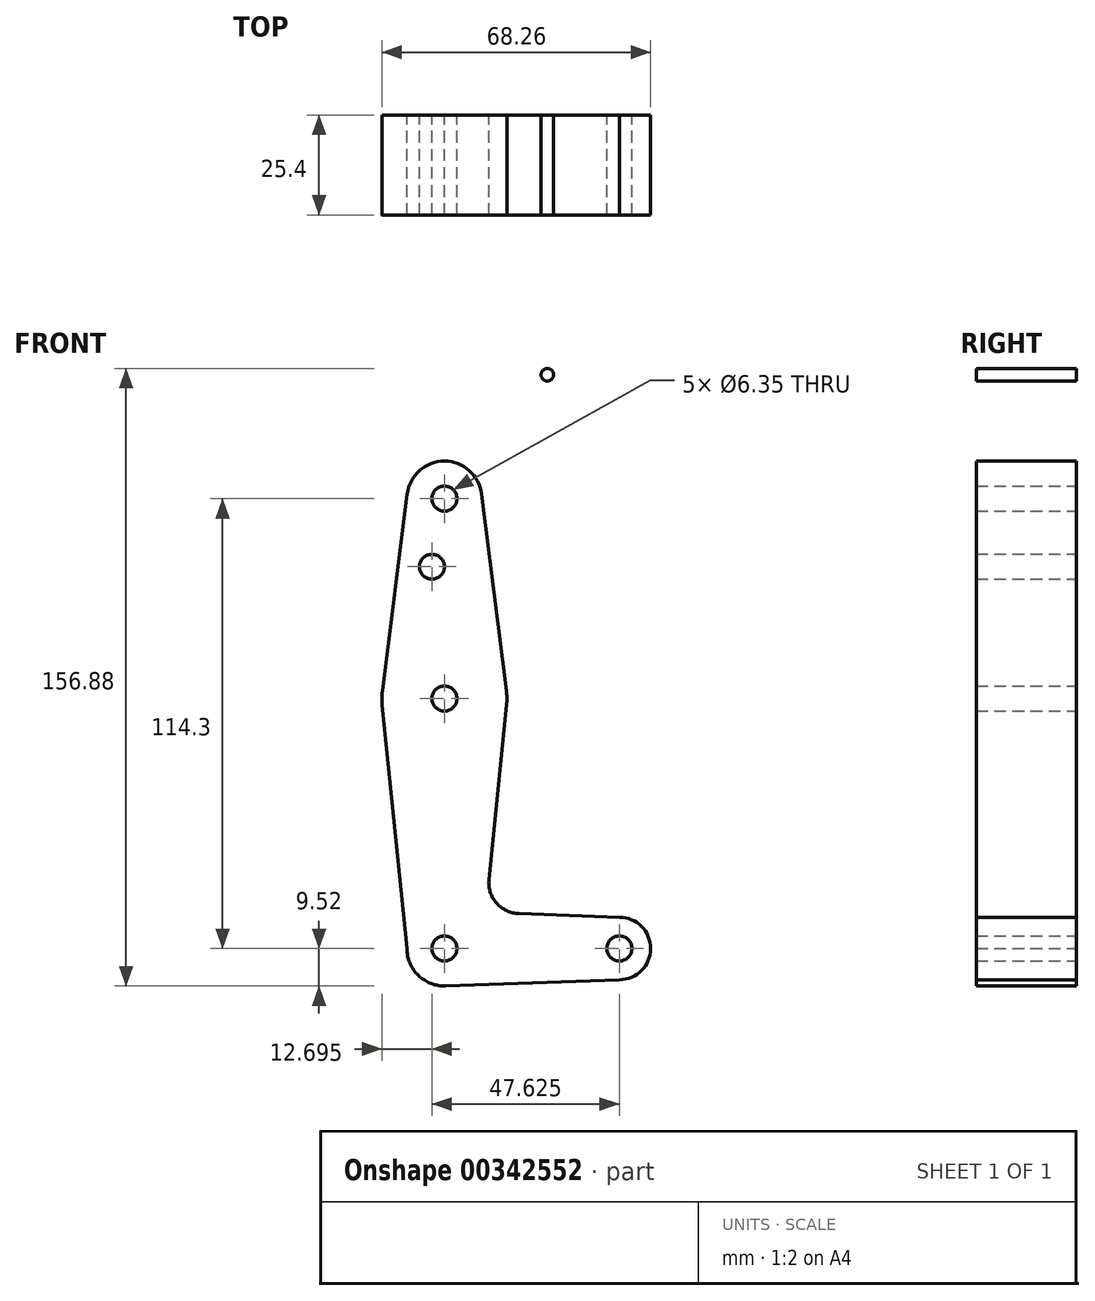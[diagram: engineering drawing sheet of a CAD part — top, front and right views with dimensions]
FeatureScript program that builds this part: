
annotation { "Feature Type Name" : "Feature", "Feature Type Description" : "" }
export const myFeature = defineFeature(function(context is Context, id is Id, definition is map)
    precondition{}
    {
        {
            var Q0;
            Q0=qCreatedBy(makeId("Front.planeOp"),FACE);
            var sketch = newSketch(context, id + "F0", { "sketchPlane" : qUnion([Q0])});
            skLineSegment(sketch, "E0", {"start": v(0, 114.3) * mm, "end": v(0, 0) * mm, "construction": true});
            skLineSegment(sketch, "E1", {"start": v(0, 0) * mm, "end": v(44.45, 0) * mm, "construction": true});
            skCircle(sketch, "E2", {"center": v(0, 114.3) * mm, "radius": 9.53 * mm});
            skCircle(sketch, "E3", {"center": v(0, 63.5) * mm, "radius": 15.88 * mm});
            skCircle(sketch, "E4", {"center": v(0, 0) * mm, "radius": 9.53 * mm});
            skCircle(sketch, "E5", {"center": v(44.45, 0) * mm, "radius": 7.94 * mm});
            skLineSegment(sketch, "E6", {"start": v(-9.53, 0) * mm, "end": v(-15.8, 61.9) * mm});
            skLineSegment(sketch, "E7", {"start": v(11.3, 17.6) * mm, "end": v(15.8, 61.9) * mm});
            skLineSegment(sketch, "E8", {"start": v(44.45, 7.94) * mm, "end": v(18.93, 8.85) * mm});
            skLineSegment(sketch, "E9", {"start": v(44.45, -7.94) * mm, "end": v(0, -9.53) * mm});
            skLineSegment(sketch, "E10", {"start": v(-15.75, 65.48) * mm, "end": v(-9.45, 115.5) * mm});
            skLineSegment(sketch, "E11", {"start": v(15.75, 65.48) * mm, "end": v(9.45, 115.5) * mm});
            skCircle(sketch, "E12", {"center": v(0, 114.3) * mm, "radius": 3.18 * mm});
            skCircle(sketch, "E13", {"center": v(26.14, 145.77) * mm, "radius": 1.59 * mm});
            skCircle(sketch, "E14", {"center": v(0, 0) * mm, "radius": 3.18 * mm});
            skCircle(sketch, "E15", {"center": v(44.45, 0) * mm, "radius": 3.18 * mm});
            skPoint(sketch, "E16.newPointB", {"position": v(0, 9.53) * mm});
            skArc(sketch, "E16.filletArc", {"start": v(11.3, 17.6) * mm, "mid": v(13.22, 11.57) * mm, "end": v(18.93, 8.85) * mm});
            skCircle(sketch, "E17", {"center": v(0, 63.5) * mm, "radius": 3.18 * mm});
            skCircle(sketch, "E18", {"center": v(-3.18, 97) * mm, "radius": 3.18 * mm});
            skSolve(sketch);
        }
        {
            var Q0;
            Q0=qSketchRegion(id+"F0",true);
            extrude(context, id + "F1", {"entities" : qUnion([Q0]), "depth" : 25.4 * mm});
        }
    });
